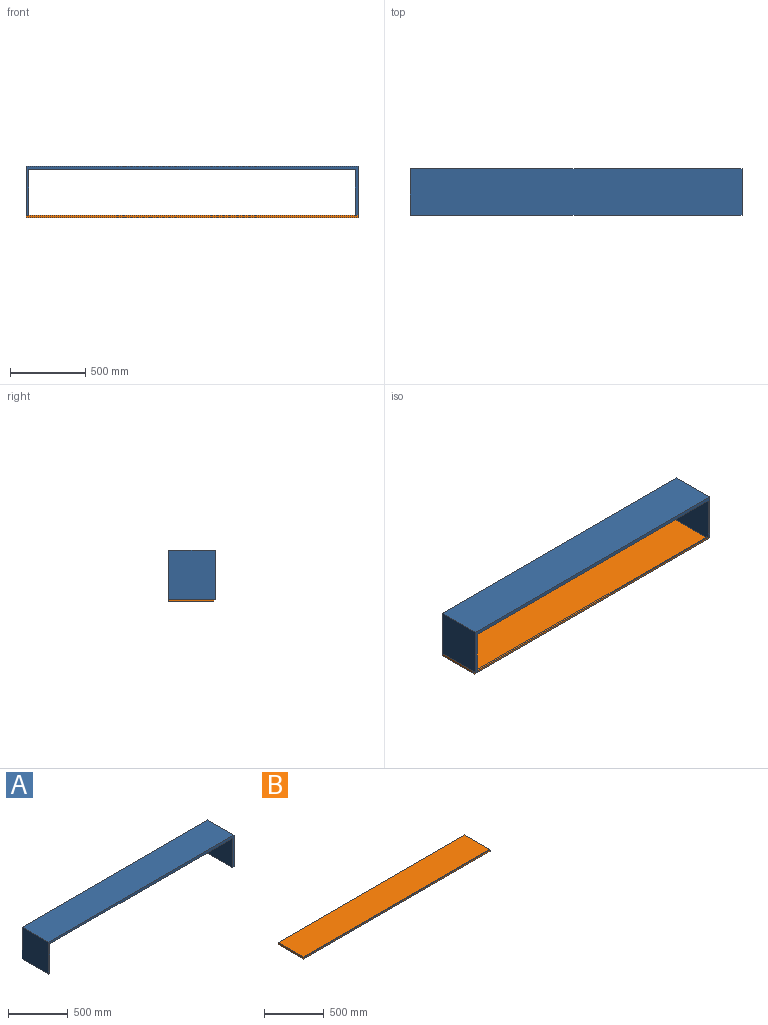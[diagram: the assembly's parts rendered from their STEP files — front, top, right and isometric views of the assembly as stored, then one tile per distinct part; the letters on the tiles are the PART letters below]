
ASSEMBLY  parts=2 mates=2
PART A: 10 faces, bbox 2200x310x325 mm
  f0: plane 2164.06x310mm, normal (0,0,-1), area 670858.7mm2, adj f1,f3,f5,f8
  f1: plane 2200x325mm, normal (0,-1,0), area 65781.9mm2, adj f0,f2,f4,f5,f6,f7,f8,f9
  f2: plane 325x310mm, normal (1,0,0), area 100750mm2, adj f1,f3,f6,f7
  f3: plane 2200x325mm, normal (0,1,0), area 65781.9mm2, adj f0,f2,f4,f5,f6,f7,f8,f9
  f4: plane 325x310mm, normal (-1,0,0), area 100750mm2, adj f1,f3,f7,f9
  f5: plane 310x300mm, normal (-1,0,0), area 93000mm2, adj f0,f1,f3,f6
  f6: plane 310x17.94mm, normal (0,0,-1), area 5561.3mm2, adj f1,f2,f3,f5
  f7: plane 2200x310mm, normal (0,0,1), area 682000mm2, adj f1,f2,f3,f4
  f8: plane 310x300mm, normal (1,0,0), area 93000mm2, adj f0,f1,f3,f9
  f9: plane 310x18mm, normal (0,0,-1), area 5580mm2, adj f1,f3,f4,f8
PART B: 7 faces, bbox 2200x300x18 mm
  f0: plane 300x18mm, normal (-1,0,0), area 5394.6mm2, adj f1,f3,f4,f5,f6
  f1: plane 2200x13mm, normal (0,-1,0), area 28600mm2, adj f0,f2,f5,f6
  f2: plane 300x18mm, normal (1,0,0), area 5394.6mm2, adj f1,f3,f4,f5,f6
  f3: plane 2200x18mm, normal (0,1,0), area 39600mm2, adj f0,f2,f4,f5
  f4: plane 2200x295mm, normal (0,0,1), area 649000mm2, adj f0,f2,f3,f6
  f5: plane 2200x300mm, normal (0,0,-1), area 660000mm2, adj f0,f1,f2,f3
  f6: cylinder r=5mm len=2200mm, axis (-1,0,0), area 17278.8mm2, adj f0,f1,f2,f4
PLACE A t=(-11.45,13.6,31.51)mm
PLACE B t=(-11.45,18.6,-286.49)mm
MATE parallel A.f7 <-> A.f2  axis (0,0,1) through (-11.45,13.6,56.51)mm
MATE fastened B.f3 <-> A.f3  axis (0,1,0) through (1088.55,168.6,-268.49)mm
